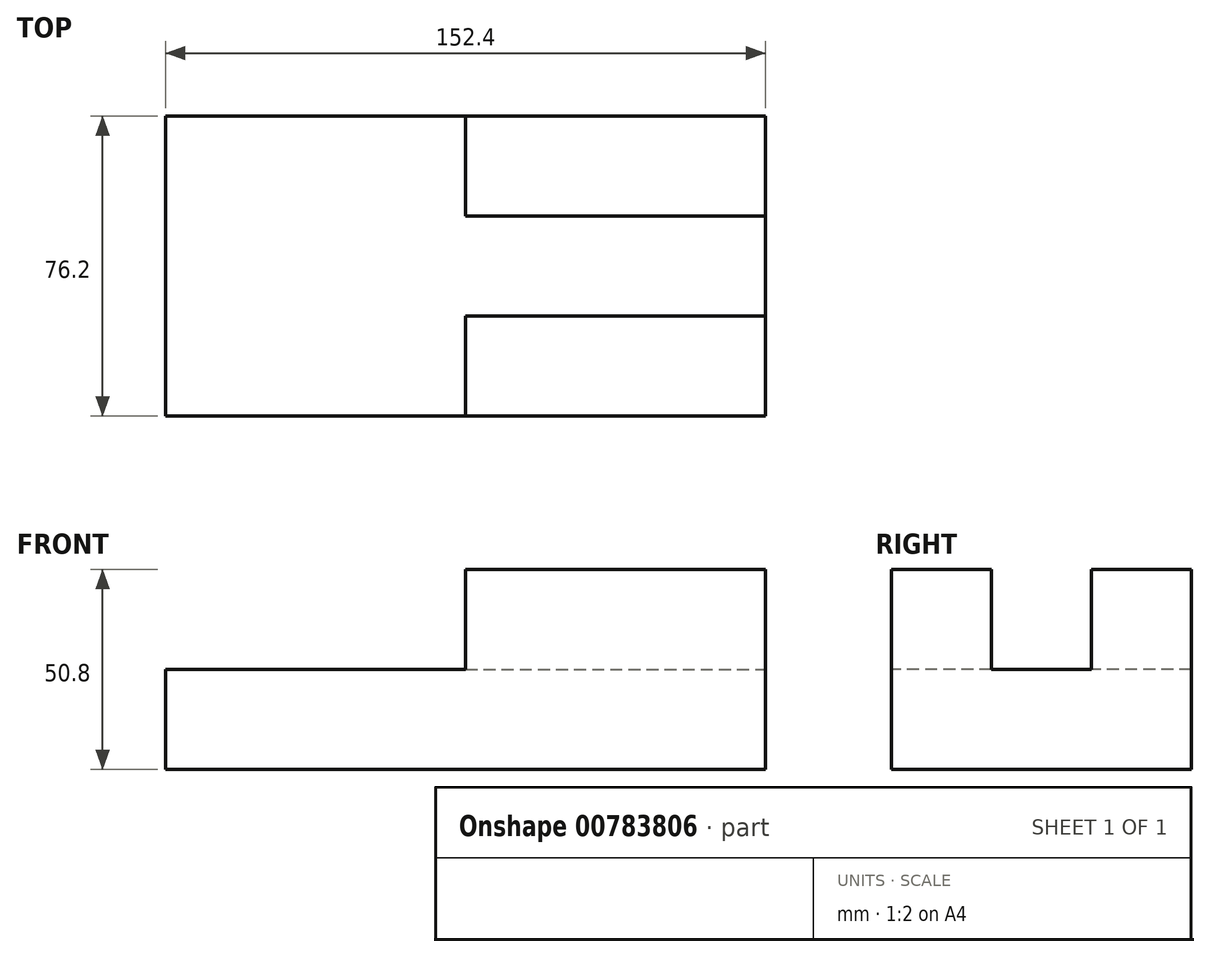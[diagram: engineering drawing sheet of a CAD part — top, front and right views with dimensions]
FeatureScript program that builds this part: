
annotation { "Feature Type Name" : "Feature", "Feature Type Description" : "" }
export const myFeature = defineFeature(function(context is Context, id is Id, definition is map)
    precondition{}
    {
        {
            var Q0;
            Q0=qCreatedBy(makeId("Front.planeOp"),FACE);
            var sketch = newSketch(context, id + "F0", { "sketchPlane" : qUnion([Q0])});
            skLineSegment(sketch, "E0", {"start": v(0, 0) * mm, "end": v(152.4, 0) * mm});
            skLineSegment(sketch, "E1", {"start": v(0, 0) * mm, "end": v(0, 50.8) * mm});
            skLineSegment(sketch, "E2", {"start": v(0, 50.8) * mm, "end": v(152.4, 50.8) * mm});
            skLineSegment(sketch, "E3", {"start": v(152.4, 50.8) * mm, "end": v(152.4, 0) * mm});
            skSolve(sketch);
        }
        {
            var Q0;
            Q0=makeQuery(id+"F0.imprint","IMPRINT",FACE,{"disambiguationData":[TD([[makeQuery(id+"F0.imprint","IMPRINT",EDGE,{"derivedFrom":sQuery(id+"F0.wireOp",EDGE,"E0")}),1.0]])]});
            extrude(context, id + "F1", {"entities" : qUnion([Q0]), "depth" : 76.2 * mm, "offsetDistance" : 25.4 * mm});
        }
        {
            var Q0;
            Q0=makeQuery(id+"F1.opExtrude","CAP_FACE",FACE,{"disambiguationData":[OSD([sQuery(id+"F0.wireOp",EDGE,"E0"),sQuery(id+"F0.wireOp",EDGE,"E1"),sQuery(id+"F0.wireOp",EDGE,"E2"),sQuery(id+"F0.wireOp",EDGE,"E3")])],"isStart":false});
            var sketch = newSketch(context, id + "F2", { "sketchPlane" : qUnion([Q0])});
            skLineSegment(sketch, "E4", {"start": v(152.4, 50.8) * mm, "end": v(76.2, 50.8) * mm});
            skLineSegment(sketch, "E5", {"start": v(76.2, 50.8) * mm, "end": v(76.2, 25.4) * mm});
            skLineSegment(sketch, "E6", {"start": v(76.2, 25.4) * mm, "end": v(0, 25.4) * mm});
            skSolve(sketch);
        }
        {
            var Q0;
            {var subQ0=sQuery(id+"F2.wireOp",EDGE,"E5");Q0=makeQuery(id+"F2.imprint","IMPRINT",FACE,{"disambiguationData":[TD([[makeQuery(id+"F2.imprint","IMPRINT",EDGE,{"derivedFrom":subQ0}),-1.0]])]});}
            extrude(context, id + "F3", {"entities" : qUnion([Q0]), "operationType" : NewBodyOperationType.REMOVE, "oppositeDirection" : true, "depth" : 76.2 * mm, "offsetDistance" : 25.4 * mm});
        }
        {
            var Q0;
            Q0=makeQuery(id+"F1.opExtrude","SWEPT_FACE",FACE,{"disambiguationData":[OSD([sQuery(id+"F0.wireOp",EDGE,"E3")])]});
            var sketch = newSketch(context, id + "F4", { "sketchPlane" : qUnion([Q0])});
            skLineSegment(sketch, "E7", {"start": v(-76.2, 0) * mm, "end": v(-50.8, 0) * mm});
            skLineSegment(sketch, "E8", {"start": v(-50.8, 0) * mm, "end": v(-50.8, 25.4) * mm});
            skLineSegment(sketch, "E9", {"start": v(-50.8, 25.4) * mm, "end": v(-25.4, 25.4) * mm});
            skLineSegment(sketch, "E10", {"start": v(-25.4, 25.4) * mm, "end": v(-25.4, 50.8) * mm});
            skLineSegment(sketch, "E11", {"start": v(-50.8, 25.4) * mm, "end": v(-50.8, 50.8) * mm});
            skLineSegment(sketch, "E12", {"start": v(-25.4, 25.4) * mm, "end": v(-25.4, 0) * mm});
            skSolve(sketch);
        }
        {
            var Q0;
            Q0=makeQuery(id+"F4.imprint","IMPRINT",FACE,{"disambiguationData":[TD([[makeQuery(id+"F4.imprint","IMPRINT",EDGE,{"derivedFrom":sQuery(id+"F4.wireOp",EDGE,"E9")}),1.0]])]});
            extrude(context, id + "F5", {"entities" : qUnion([Q0]), "operationType" : NewBodyOperationType.REMOVE, "oppositeDirection" : true, "depth" : 76.2 * mm, "offsetDistance" : 25.4 * mm});
        }
    });
